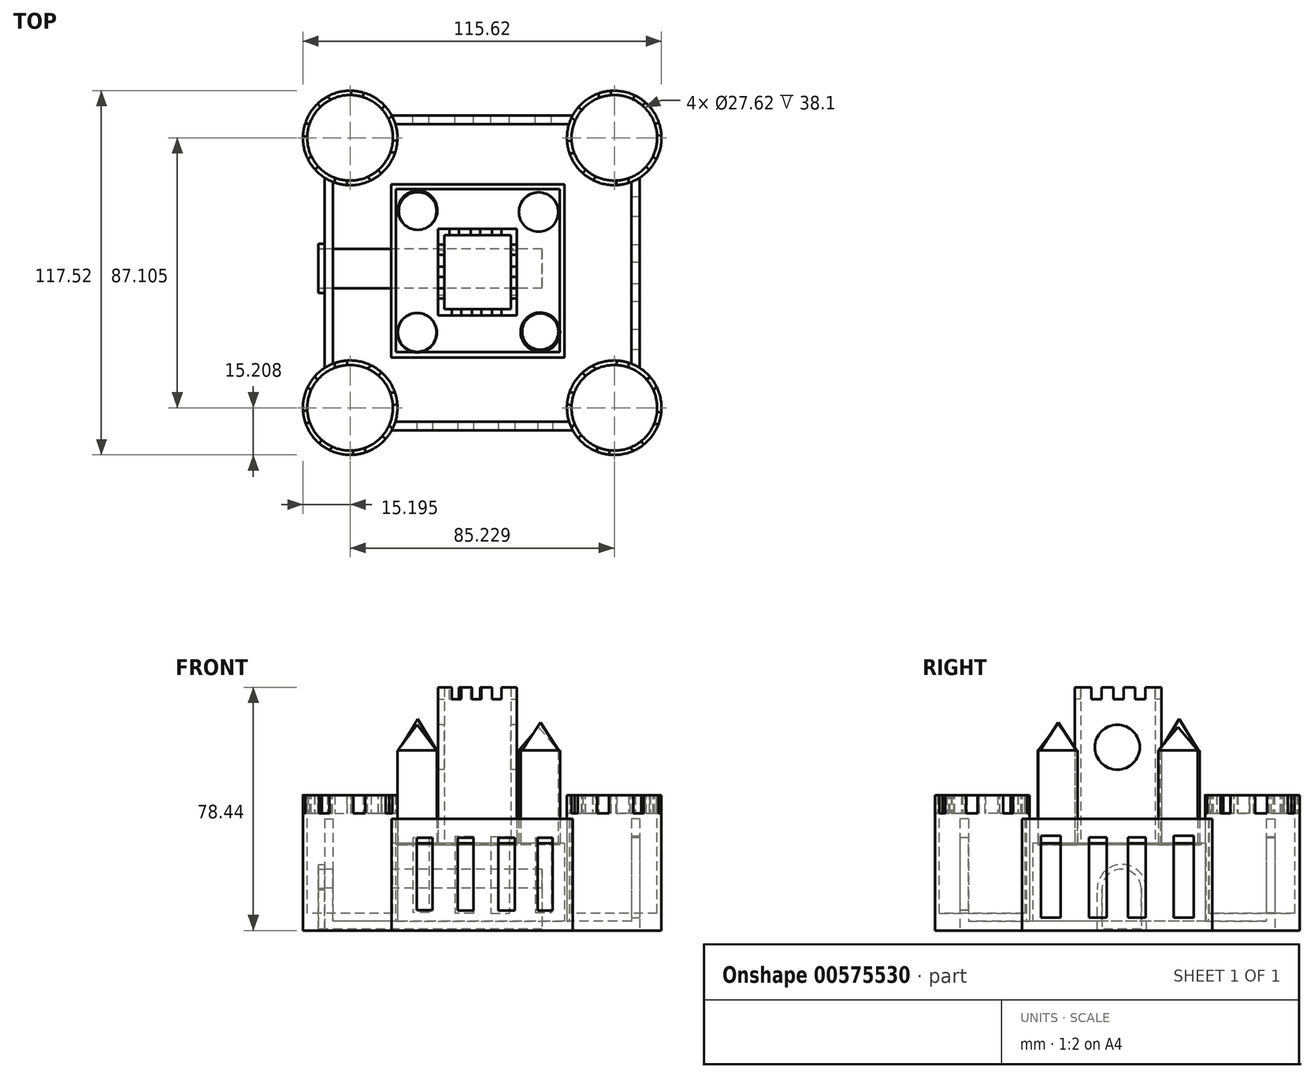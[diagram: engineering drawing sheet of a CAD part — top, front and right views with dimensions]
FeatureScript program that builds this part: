
annotation { "Feature Type Name" : "Feature", "Feature Type Description" : "" }
export const myFeature = defineFeature(function(context is Context, id is Id, definition is map)
    precondition{}
    {
        {
            var Q0;
            Q0=qCreatedBy(makeId("Top.planeOp"),FACE);
            var sketch = newSketch(context, id + "F0", { "sketchPlane" : qUnion([Q0])});
            skLineSegment(sketch, "E0.bottom", {"start": v(29.19, -50.8) * mm, "end": v(-29.19, -50.8) * mm});
            skLineSegment(sketch, "E0.top", {"start": v(29.19, 50.8) * mm, "end": v(-29.19, 50.8) * mm});
            skLineSegment(sketch, "E0.left", {"start": v(50.8, -30.7) * mm, "end": v(50.8, 30.7) * mm});
            skLineSegment(sketch, "E0.right", {"start": v(-50.8, -30.7) * mm, "end": v(-50.8, 30.7) * mm});
            skPoint(sketch, "E0.middle", {"position": v(0, 0) * mm});
            skCircle(sketch, "E1", {"center": v(-42.57, 43.52) * mm, "radius": 15.24 * mm});
            skCircle(sketch, "E2.MirrorC", {"center": v(42.57, 43.52) * mm, "radius": 15.24 * mm});
            skCircle(sketch, "E3.MirrorC", {"center": v(-42.57, -43.52) * mm, "radius": 15.24 * mm});
            skCircle(sketch, "E4.MirrorC", {"center": v(42.57, -43.52) * mm, "radius": 15.24 * mm});
            skPoint(sketch, "E5.orphan", {"position": v(-50.8, 50.8) * mm});
            skPoint(sketch, "E6.orphan", {"position": v(-50.8, -50.8) * mm});
            skPoint(sketch, "E7.orphan", {"position": v(50.8, -50.8) * mm});
            skPoint(sketch, "E8.orphan", {"position": v(50.8, 50.8) * mm});
            skSolve(sketch);
        }
        {
            var Q0;
            Q0 = qSketchRegion(id + "F0", true);
            extrude(context, id + "F1", {"entities" : qUnion([Q0]), "depth" : 3 * mm, "offsetDistance" : 25.4 * mm});
        }
        {
            var Q0;
            Q0=makeQuery(id+"F1.opExtrude","CAP_FACE",FACE,{"disambiguationData":[OSD([sQuery(id+"F0.wireOp",EDGE,"E0.bottom"),sQuery(id+"F0.wireOp",EDGE,"E0.top"),sQuery(id+"F0.wireOp",EDGE,"E0.left"),sQuery(id+"F0.wireOp",EDGE,"E0.right"),sQuery(id+"F0.wireOp",EDGE,"E1"),sQuery(id+"F0.wireOp",EDGE,"E2.MirrorC"),sQuery(id+"F0.wireOp",EDGE,"E3.MirrorC"),sQuery(id+"F0.wireOp",EDGE,"E4.MirrorC")])],"isStart":false});
            var sketch = newSketch(context, id + "F2", { "sketchPlane" : qUnion([Q0])});
            skCircle(sketch, "E9", {"center": v(-42.57, 43.52) * mm, "radius": 15.24 * mm});
            skCircle(sketch, "E10.MirrorC", {"center": v(42.57, 43.52) * mm, "radius": 15.24 * mm});
            skCircle(sketch, "E11.MirrorC", {"center": v(-42.57, -43.52) * mm, "radius": 15.24 * mm});
            skCircle(sketch, "E12.MirrorC", {"center": v(42.57, -43.52) * mm, "radius": 15.24 * mm});
            skSolve(sketch);
        }
        {
            var Q0;
            Q0 = qSketchRegion(id + "F2", true);
            extrude(context, id + "F3", {"entities" : qUnion([Q0]), "operationType" : NewBodyOperationType.ADD, "depth" : 40.64 * mm, "offsetDistance" : 25.4 * mm});
        }
        {
            var Q0;
            Q0=makeQuery(id+"F1.opExtrude","CAP_FACE",FACE,{"disambiguationData":[OSD([sQuery(id+"F0.wireOp",EDGE,"E0.bottom"),sQuery(id+"F0.wireOp",EDGE,"E0.top"),sQuery(id+"F0.wireOp",EDGE,"E0.left"),sQuery(id+"F0.wireOp",EDGE,"E0.right"),sQuery(id+"F0.wireOp",EDGE,"E1"),sQuery(id+"F0.wireOp",EDGE,"E2.MirrorC"),sQuery(id+"F0.wireOp",EDGE,"E3.MirrorC"),sQuery(id+"F0.wireOp",EDGE,"E4.MirrorC")])],"isStart":false});
            var sketch = newSketch(context, id + "F4", { "sketchPlane" : qUnion([Q0])});
            skArc(sketch, "E13", {"start": v(-29.19, -50.8) * mm, "mid": v(-28.53, -49.45) * mm, "end": v(-28.02, -48.04) * mm});
            skArc(sketch, "E14.MirrorCS", {"start": v(29.19, -50.8) * mm, "mid": v(28.53, -49.45) * mm, "end": v(28.02, -48.04) * mm});
            skLineSegment(sketch, "E15", {"start": v(-29.19, -50.8) * mm, "end": v(29.19, -50.8) * mm});
            skLineSegment(sketch, "E16", {"start": v(-28.02, -48.04) * mm, "end": v(28.02, -48.04) * mm});
            skLineSegment(sketch, "E17.MirrorCS", {"start": v(-28.02, 48.04) * mm, "end": v(28.02, 48.04) * mm});
            skLineSegment(sketch, "E18.MirrorCS", {"start": v(-29.19, 50.8) * mm, "end": v(29.19, 50.8) * mm});
            skArc(sketch, "E19.MirrorCS", {"start": v(29.19, 50.8) * mm, "mid": v(28.53, 49.45) * mm, "end": v(28.02, 48.04) * mm});
            skArc(sketch, "E20.MirrorCS", {"start": v(-29.19, 50.8) * mm, "mid": v(-28.53, 49.45) * mm, "end": v(-28.02, 48.04) * mm});
            skArc(sketch, "E21.trimOffspring", {"start": v(-48.13, -29.33) * mm, "mid": v(-49.5, -29.94) * mm, "end": v(-50.8, -30.7) * mm});
            skArc(sketch, "E22.MirrorCS", {"start": v(-48.13, 29.33) * mm, "mid": v(-49.5, 29.94) * mm, "end": v(-50.8, 30.7) * mm});
            skLineSegment(sketch, "E23", {"start": v(-50.8, 30.7) * mm, "end": v(-50.8, -30.7) * mm});
            skLineSegment(sketch, "E24", {"start": v(-48.13, 29.33) * mm, "end": v(-48.13, -29.33) * mm});
            skLineSegment(sketch, "E25.MirrorCS", {"start": v(48.13, 29.33) * mm, "end": v(48.13, -29.33) * mm});
            skLineSegment(sketch, "E26.MirrorCS", {"start": v(50.8, 30.7) * mm, "end": v(50.8, -30.7) * mm});
            skArc(sketch, "E27.MirrorCS", {"start": v(48.13, -29.33) * mm, "mid": v(49.5, -29.94) * mm, "end": v(50.8, -30.7) * mm});
            skArc(sketch, "E28.MirrorCS", {"start": v(48.13, 29.33) * mm, "mid": v(49.5, 29.94) * mm, "end": v(50.8, 30.7) * mm});
            skSolve(sketch);
        }
        {
            var Q0;
            Q0 = qSketchRegion(id + "F4", true);
            extrude(context, id + "F5", {"entities" : qUnion([Q0]), "operationType" : NewBodyOperationType.ADD, "depth" : 33.02 * mm, "offsetDistance" : 25.4 * mm});
        }
        {
            var Q0;
            Q0=makeQuery(id+"F3.opExtrude","CAP_FACE",FACE,{"disambiguationData":[OSD([sQuery(id+"F2.wireOp",EDGE,"E10.MirrorC")])],"isStart":false});
            var sketch = newSketch(context, id + "F6", { "sketchPlane" : qUnion([Q0])});
            skPoint(sketch, "E29.first.point", {"position": v(-57.88, 42.89) * mm});
            skPoint(sketch, "E29.second.point", {"position": v(-27.36, 44.4) * mm});
            skPoint(sketch, "E29.third.point", {"position": v(-44.7, 28.42) * mm});
            skCircle(sketch, "E30", {"center": v(-42.61, 43.55) * mm, "radius": 13.8 * mm});
            skCircle(sketch, "E31.MirrorC", {"center": v(-42.61, -43.55) * mm, "radius": 13.8 * mm});
            skCircle(sketch, "E32.MirrorC", {"center": v(42.61, 43.55) * mm, "radius": 13.8 * mm});
            skCircle(sketch, "E33.MirrorC", {"center": v(42.61, -43.55) * mm, "radius": 13.8 * mm});
            skSolve(sketch);
        }
        {
            var Q0;
            Q0 = qSketchRegion(id + "F6", true);
            extrude(context, id + "F7", {"entities" : qUnion([Q0]), "operationType" : NewBodyOperationType.REMOVE, "oppositeDirection" : true, "depth" : 38.1 * mm, "offsetDistance" : 25.4 * mm});
        }
        {
            var Q0;
            Q0=makeQuery(id+"F3.opExtrude","CAP_FACE",FACE,{"disambiguationData":[OSD([sQuery(id+"F2.wireOp",EDGE,"E11.MirrorC")])],"isStart":false});
            var sketch = newSketch(context, id + "F8", { "sketchPlane" : qUnion([Q0])});
            skLineSegment(sketch, "E34", {"start": v(-47.54, -28.27) * mm, "end": v(-47.54, -31.48) * mm});
            skLineSegment(sketch, "E35", {"start": v(-47.54, -31.48) * mm, "end": v(-43.3, -30.83) * mm});
            skLineSegment(sketch, "E36", {"start": v(-43.3, -30.83) * mm, "end": v(-43.78, -27.75) * mm});
            skLineSegment(sketch, "E37", {"start": v(-43.78, -27.75) * mm, "end": v(-47.54, -28.27) * mm});
            skLineSegment(sketch, "E38.1.0", {"start": v(-54.6, -33.2) * mm, "end": v(-56.9, -36.23) * mm});
            skLineSegment(sketch, "E38.1.1", {"start": v(-54.63, -38.5) * mm, "end": v(-52.1, -35.05) * mm});
            skLineSegment(sketch, "E38.1.2", {"start": v(-56.9, -36.23) * mm, "end": v(-54.63, -38.5) * mm});
            skLineSegment(sketch, "E38.1.3", {"start": v(-52.1, -35.05) * mm, "end": v(-54.6, -33.2) * mm});
            skLineSegment(sketch, "E38.2.0", {"start": v(-58.41, -44.72) * mm, "end": v(-57.9, -48.48) * mm});
            skLineSegment(sketch, "E38.2.1", {"start": v(-54.68, -48.48) * mm, "end": v(-55.33, -44.24) * mm});
            skLineSegment(sketch, "E38.2.2", {"start": v(-57.9, -48.48) * mm, "end": v(-54.68, -48.48) * mm});
            skLineSegment(sketch, "E38.2.3", {"start": v(-55.33, -44.24) * mm, "end": v(-58.41, -44.72) * mm});
            skLineSegment(sketch, "E38.3.0", {"start": v(-52.96, -55.55) * mm, "end": v(-49.94, -57.84) * mm});
            skLineSegment(sketch, "E38.3.1", {"start": v(-47.67, -55.57) * mm, "end": v(-51.12, -53.03) * mm});
            skLineSegment(sketch, "E38.3.2", {"start": v(-49.94, -57.84) * mm, "end": v(-47.67, -55.57) * mm});
            skLineSegment(sketch, "E38.3.3", {"start": v(-51.12, -53.03) * mm, "end": v(-52.96, -55.55) * mm});
            skLineSegment(sketch, "E38.4.0", {"start": v(-41.45, -59.35) * mm, "end": v(-37.69, -58.83) * mm});
            skLineSegment(sketch, "E38.4.1", {"start": v(-37.69, -55.62) * mm, "end": v(-41.92, -56.27) * mm});
            skLineSegment(sketch, "E38.4.2", {"start": v(-37.69, -58.83) * mm, "end": v(-37.69, -55.62) * mm});
            skLineSegment(sketch, "E38.4.3", {"start": v(-41.92, -56.27) * mm, "end": v(-41.45, -59.35) * mm});
            skLineSegment(sketch, "E38.5.0", {"start": v(-30.62, -53.9) * mm, "end": v(-28.33, -50.87) * mm});
            skLineSegment(sketch, "E38.5.1", {"start": v(-30.6, -48.6) * mm, "end": v(-33.13, -52.06) * mm});
            skLineSegment(sketch, "E38.5.2", {"start": v(-28.33, -50.87) * mm, "end": v(-30.6, -48.6) * mm});
            skLineSegment(sketch, "E38.5.3", {"start": v(-33.13, -52.06) * mm, "end": v(-30.62, -53.9) * mm});
            skLineSegment(sketch, "E38.6.0", {"start": v(-26.82, -42.39) * mm, "end": v(-27.33, -38.63) * mm});
            skLineSegment(sketch, "E38.6.1", {"start": v(-30.55, -38.63) * mm, "end": v(-29.9, -42.86) * mm});
            skLineSegment(sketch, "E38.6.2", {"start": v(-27.33, -38.63) * mm, "end": v(-30.55, -38.63) * mm});
            skLineSegment(sketch, "E38.6.3", {"start": v(-29.9, -42.86) * mm, "end": v(-26.82, -42.39) * mm});
            skLineSegment(sketch, "E38.7.0", {"start": v(-32.27, -31.56) * mm, "end": v(-35.3, -29.26) * mm});
            skLineSegment(sketch, "E38.7.1", {"start": v(-37.56, -31.54) * mm, "end": v(-34.1, -34.07) * mm});
            skLineSegment(sketch, "E38.7.2", {"start": v(-35.3, -29.26) * mm, "end": v(-37.56, -31.54) * mm});
            skLineSegment(sketch, "E38.7.3", {"start": v(-34.1, -34.07) * mm, "end": v(-32.27, -31.56) * mm});
            skPoint(sketch, "E38.center", {"position": v(-42.61, -43.55) * mm});
            skLineSegment(sketch, "E39.MirrorCS", {"start": v(-47.54, 31.48) * mm, "end": v(-43.3, 30.83) * mm});
            skLineSegment(sketch, "E40.MirrorCS", {"start": v(-43.78, 27.75) * mm, "end": v(-47.54, 28.27) * mm});
            skLineSegment(sketch, "E41.MirrorCS", {"start": v(-43.3, 30.83) * mm, "end": v(-43.78, 27.75) * mm});
            skLineSegment(sketch, "E42.MirrorCS", {"start": v(-47.54, 28.27) * mm, "end": v(-47.54, 31.48) * mm});
            skLineSegment(sketch, "E43.MirrorCS", {"start": v(26.82, -42.39) * mm, "end": v(27.33, -38.63) * mm});
            skLineSegment(sketch, "E44.MirrorCS", {"start": v(30.55, -38.63) * mm, "end": v(29.9, -42.86) * mm});
            skLineSegment(sketch, "E45.MirrorCS", {"start": v(29.9, -42.86) * mm, "end": v(26.82, -42.39) * mm});
            skLineSegment(sketch, "E46.MirrorCS", {"start": v(27.33, -38.63) * mm, "end": v(30.55, -38.63) * mm});
            skLineSegment(sketch, "E47.MirrorCS", {"start": v(27.33, 38.63) * mm, "end": v(30.55, 38.63) * mm});
            skLineSegment(sketch, "E48.MirrorCS", {"start": v(29.9, 42.86) * mm, "end": v(26.82, 42.39) * mm});
            skLineSegment(sketch, "E49.MirrorCS", {"start": v(30.55, 38.63) * mm, "end": v(29.9, 42.86) * mm});
            skLineSegment(sketch, "E50.MirrorCS", {"start": v(26.82, 42.39) * mm, "end": v(27.33, 38.63) * mm});
            skLineSegment(sketch, "E51.1.0", {"start": v(32.9, -51.78) * mm, "end": v(30.4, -53.62) * mm});
            skLineSegment(sketch, "E51.1.1", {"start": v(30.4, -53.62) * mm, "end": v(28.1, -50.6) * mm});
            skLineSegment(sketch, "E51.1.2", {"start": v(30.37, -48.32) * mm, "end": v(32.9, -51.78) * mm});
            skLineSegment(sketch, "E51.1.3", {"start": v(28.1, -50.6) * mm, "end": v(30.37, -48.32) * mm});
            skLineSegment(sketch, "E51.2.0", {"start": v(41.34, -55.96) * mm, "end": v(40.87, -59.04) * mm});
            skLineSegment(sketch, "E51.2.1", {"start": v(40.87, -59.04) * mm, "end": v(37.1, -58.52) * mm});
            skLineSegment(sketch, "E51.2.2", {"start": v(37.1, -55.3) * mm, "end": v(41.34, -55.96) * mm});
            skLineSegment(sketch, "E51.2.3", {"start": v(37.1, -58.52) * mm, "end": v(37.1, -55.3) * mm});
            skLineSegment(sketch, "E51.3.0", {"start": v(50.26, -52.95) * mm, "end": v(52.1, -55.46) * mm});
            skLineSegment(sketch, "E51.3.1", {"start": v(52.1, -55.46) * mm, "end": v(49.07, -57.75) * mm});
            skLineSegment(sketch, "E51.3.2", {"start": v(46.8, -55.48) * mm, "end": v(50.26, -52.95) * mm});
            skLineSegment(sketch, "E51.3.3", {"start": v(49.07, -57.75) * mm, "end": v(46.8, -55.48) * mm});
            skLineSegment(sketch, "E51.4.0", {"start": v(54.43, -44.51) * mm, "end": v(57.51, -44.99) * mm});
            skLineSegment(sketch, "E51.4.2", {"start": v(53.78, -48.75) * mm, "end": v(54.43, -44.51) * mm});
            skLineSegment(sketch, "E51.4.3", {"start": v(57, -48.75) * mm, "end": v(53.78, -48.75) * mm});
            skLineSegment(sketch, "E51.5.0", {"start": v(51.42, -35.6) * mm, "end": v(53.93, -33.75) * mm});
            skLineSegment(sketch, "E51.5.2", {"start": v(53.96, -39.05) * mm, "end": v(51.42, -35.6) * mm});
            skLineSegment(sketch, "E51.5.3", {"start": v(56.23, -36.78) * mm, "end": v(53.96, -39.05) * mm});
            skLineSegment(sketch, "E51.6.0", {"start": v(42.99, -31.42) * mm, "end": v(43.46, -28.34) * mm});
            skLineSegment(sketch, "E51.6.2", {"start": v(47.23, -32.07) * mm, "end": v(42.99, -31.42) * mm});
            skLineSegment(sketch, "E51.6.3", {"start": v(47.23, -28.86) * mm, "end": v(47.23, -32.07) * mm});
            skLineSegment(sketch, "E51.7.0", {"start": v(34.07, -34.43) * mm, "end": v(32.23, -31.92) * mm});
            skLineSegment(sketch, "E51.7.1", {"start": v(32.23, -31.92) * mm, "end": v(35.26, -29.62) * mm});
            skLineSegment(sketch, "E51.7.2", {"start": v(37.53, -31.9) * mm, "end": v(34.07, -34.43) * mm});
            skLineSegment(sketch, "E51.7.3", {"start": v(35.26, -29.62) * mm, "end": v(37.53, -31.9) * mm});
            skPoint(sketch, "E51.center", {"position": v(42.16, -43.69) * mm});
            skLineSegment(sketch, "E52.1.0", {"start": v(32.12, 31.66) * mm, "end": v(35.15, 29.37) * mm});
            skLineSegment(sketch, "E52.1.1", {"start": v(37.42, 31.64) * mm, "end": v(33.97, 34.17) * mm});
            skLineSegment(sketch, "E52.1.2", {"start": v(33.97, 34.17) * mm, "end": v(32.12, 31.66) * mm});
            skLineSegment(sketch, "E52.1.3", {"start": v(35.15, 29.37) * mm, "end": v(37.42, 31.64) * mm});
            skLineSegment(sketch, "E52.2.0", {"start": v(43.46, 27.83) * mm, "end": v(47.23, 28.35) * mm});
            skLineSegment(sketch, "E52.2.1", {"start": v(47.23, 31.56) * mm, "end": v(42.99, 30.91) * mm});
            skLineSegment(sketch, "E52.2.2", {"start": v(42.99, 30.91) * mm, "end": v(43.46, 27.83) * mm});
            skLineSegment(sketch, "E52.2.3", {"start": v(47.23, 28.35) * mm, "end": v(47.23, 31.56) * mm});
            skLineSegment(sketch, "E52.3.0", {"start": v(54.19, 33.14) * mm, "end": v(56.48, 36.17) * mm});
            skLineSegment(sketch, "E52.3.1", {"start": v(54.21, 38.44) * mm, "end": v(51.68, 34.98) * mm});
            skLineSegment(sketch, "E52.3.2", {"start": v(51.68, 34.98) * mm, "end": v(54.19, 33.14) * mm});
            skLineSegment(sketch, "E52.3.3", {"start": v(56.48, 36.17) * mm, "end": v(54.21, 38.44) * mm});
            skLineSegment(sketch, "E52.4.0", {"start": v(58.02, 44.48) * mm, "end": v(57.5, 48.24) * mm});
            skLineSegment(sketch, "E52.4.1", {"start": v(54.3, 48.24) * mm, "end": v(54.94, 44) * mm});
            skLineSegment(sketch, "E52.4.2", {"start": v(54.94, 44) * mm, "end": v(58.02, 44.48) * mm});
            skLineSegment(sketch, "E52.4.3", {"start": v(57.5, 48.24) * mm, "end": v(54.3, 48.24) * mm});
            skLineSegment(sketch, "E52.5.0", {"start": v(52.71, 55.2) * mm, "end": v(49.68, 57.5) * mm});
            skLineSegment(sketch, "E52.5.1", {"start": v(47.41, 55.23) * mm, "end": v(50.87, 52.7) * mm});
            skLineSegment(sketch, "E52.5.2", {"start": v(50.87, 52.7) * mm, "end": v(52.71, 55.2) * mm});
            skLineSegment(sketch, "E52.5.3", {"start": v(49.68, 57.5) * mm, "end": v(47.41, 55.23) * mm});
            skLineSegment(sketch, "E52.6.0", {"start": v(41.37, 59.04) * mm, "end": v(37.61, 58.52) * mm});
            skLineSegment(sketch, "E52.6.1", {"start": v(37.61, 55.3) * mm, "end": v(41.85, 55.96) * mm});
            skLineSegment(sketch, "E52.6.2", {"start": v(41.85, 55.96) * mm, "end": v(41.37, 59.04) * mm});
            skLineSegment(sketch, "E52.6.3", {"start": v(37.61, 58.52) * mm, "end": v(37.61, 55.3) * mm});
            skLineSegment(sketch, "E52.7.0", {"start": v(30.65, 53.73) * mm, "end": v(28.35, 50.7) * mm});
            skLineSegment(sketch, "E52.7.1", {"start": v(30.62, 48.43) * mm, "end": v(33.16, 51.89) * mm});
            skLineSegment(sketch, "E52.7.2", {"start": v(33.16, 51.89) * mm, "end": v(30.65, 53.73) * mm});
            skLineSegment(sketch, "E52.7.3", {"start": v(28.35, 50.7) * mm, "end": v(30.62, 48.43) * mm});
            skPoint(sketch, "E52.center", {"position": v(42.42, 43.43) * mm});
            skLineSegment(sketch, "E53.1.0", {"start": v(-35.47, 29.45) * mm, "end": v(-37.74, 31.72) * mm});
            skLineSegment(sketch, "E53.1.1", {"start": v(-34.28, 34.26) * mm, "end": v(-32.44, 31.74) * mm});
            skLineSegment(sketch, "E53.1.2", {"start": v(-32.44, 31.74) * mm, "end": v(-35.47, 29.45) * mm});
            skLineSegment(sketch, "E53.1.3", {"start": v(-37.74, 31.72) * mm, "end": v(-34.28, 34.26) * mm});
            skLineSegment(sketch, "E53.2.0", {"start": v(-27.76, 38.82) * mm, "end": v(-30.98, 38.82) * mm});
            skLineSegment(sketch, "E53.2.1", {"start": v(-30.32, 43.06) * mm, "end": v(-27.25, 42.58) * mm});
            skLineSegment(sketch, "E53.2.2", {"start": v(-27.25, 42.58) * mm, "end": v(-27.76, 38.82) * mm});
            skLineSegment(sketch, "E53.2.3", {"start": v(-30.98, 38.82) * mm, "end": v(-30.32, 43.06) * mm});
            skLineSegment(sketch, "E53.3.0", {"start": v(-28.94, 50.9) * mm, "end": v(-31.21, 48.62) * mm});
            skLineSegment(sketch, "E53.3.1", {"start": v(-33.75, 52.08) * mm, "end": v(-31.24, 53.92) * mm});
            skLineSegment(sketch, "E53.3.2", {"start": v(-31.24, 53.92) * mm, "end": v(-28.94, 50.9) * mm});
            skLineSegment(sketch, "E53.3.3", {"start": v(-31.21, 48.62) * mm, "end": v(-33.75, 52.08) * mm});
            skLineSegment(sketch, "E53.4.0", {"start": v(-38.31, 58.6) * mm, "end": v(-38.31, 55.38) * mm});
            skLineSegment(sketch, "E53.4.1", {"start": v(-42.55, 56.04) * mm, "end": v(-42.07, 59.11) * mm});
            skLineSegment(sketch, "E53.4.2", {"start": v(-42.07, 59.11) * mm, "end": v(-38.31, 58.6) * mm});
            skLineSegment(sketch, "E53.4.3", {"start": v(-38.31, 55.38) * mm, "end": v(-42.55, 56.04) * mm});
            skLineSegment(sketch, "E53.5.0", {"start": v(-50.38, 57.42) * mm, "end": v(-48.11, 55.15) * mm});
            skLineSegment(sketch, "E53.5.1", {"start": v(-51.57, 52.61) * mm, "end": v(-53.41, 55.12) * mm});
            skLineSegment(sketch, "E53.5.2", {"start": v(-53.41, 55.12) * mm, "end": v(-50.38, 57.42) * mm});
            skLineSegment(sketch, "E53.5.3", {"start": v(-48.11, 55.15) * mm, "end": v(-51.57, 52.61) * mm});
            skLineSegment(sketch, "E53.6.0", {"start": v(-58.09, 48.05) * mm, "end": v(-54.88, 48.05) * mm});
            skLineSegment(sketch, "E53.6.1", {"start": v(-55.53, 43.81) * mm, "end": v(-58.6, 44.29) * mm});
            skLineSegment(sketch, "E53.6.2", {"start": v(-58.6, 44.29) * mm, "end": v(-58.09, 48.05) * mm});
            skLineSegment(sketch, "E53.6.3", {"start": v(-54.88, 48.05) * mm, "end": v(-55.53, 43.81) * mm});
            skLineSegment(sketch, "E53.7.0", {"start": v(-56.9, 35.98) * mm, "end": v(-54.64, 38.25) * mm});
            skLineSegment(sketch, "E53.7.1", {"start": v(-52.1, 34.8) * mm, "end": v(-54.62, 32.95) * mm});
            skLineSegment(sketch, "E53.7.2", {"start": v(-54.62, 32.95) * mm, "end": v(-56.9, 35.98) * mm});
            skLineSegment(sketch, "E53.7.3", {"start": v(-54.64, 38.25) * mm, "end": v(-52.1, 34.8) * mm});
            skPoint(sketch, "E53.center", {"position": v(-42.93, 43.43) * mm});
            skLineSegment(sketch, "E54", {"start": v(57, -48.75) * mm, "end": v(60.9, -48.75) * mm});
            skLineSegment(sketch, "E55", {"start": v(60.9, -48.75) * mm, "end": v(60.87, -45.44) * mm});
            skLineSegment(sketch, "E56", {"start": v(60.87, -45.44) * mm, "end": v(57.51, -44.99) * mm});
            skLineSegment(sketch, "E57", {"start": v(56.23, -36.78) * mm, "end": v(62.09, -33.6) * mm});
            skLineSegment(sketch, "E58", {"start": v(62.09, -33.6) * mm, "end": v(58.77, -31.36) * mm});
            skLineSegment(sketch, "E59", {"start": v(58.77, -31.36) * mm, "end": v(53.93, -33.75) * mm});
            skLineSegment(sketch, "E60", {"start": v(47.23, -28.86) * mm, "end": v(43.42, -20.08) * mm});
            skLineSegment(sketch, "E61", {"start": v(43.42, -20.08) * mm, "end": v(43.46, -28.34) * mm});
            skSolve(sketch);
        }
        {
            var Q0;
            Q0 = qSketchRegion(id + "F8", true);
            extrude(context, id + "F9", {"entities" : qUnion([Q0]), "operationType" : NewBodyOperationType.REMOVE, "oppositeDirection" : true, "depth" : 5.84 * mm, "offsetDistance" : 25.4 * mm});
        }
        {
            var Q0;
            Q0=makeQuery(id+"F1.opExtrude","CAP_FACE",FACE,{"disambiguationData":[OSD([sQuery(id+"F0.wireOp",EDGE,"E0.bottom"),sQuery(id+"F0.wireOp",EDGE,"E0.top"),sQuery(id+"F0.wireOp",EDGE,"E0.left"),sQuery(id+"F0.wireOp",EDGE,"E0.right"),sQuery(id+"F0.wireOp",EDGE,"E1"),sQuery(id+"F0.wireOp",EDGE,"E2.MirrorC"),sQuery(id+"F0.wireOp",EDGE,"E3.MirrorC"),sQuery(id+"F0.wireOp",EDGE,"E4.MirrorC")])],"isStart":false});
            var sketch = newSketch(context, id + "F10", { "sketchPlane" : qUnion([Q0])});
            skLineSegment(sketch, "E62.bottom", {"start": v(26.57, 28.58) * mm, "end": v(-29.31, 28.58) * mm});
            skLineSegment(sketch, "E62.top", {"start": v(26.57, -27.3) * mm, "end": v(-29.31, -27.3) * mm});
            skLineSegment(sketch, "E62.left", {"start": v(26.57, 28.58) * mm, "end": v(26.57, -27.3) * mm});
            skLineSegment(sketch, "E62.right", {"start": v(-29.31, 28.58) * mm, "end": v(-29.31, -27.3) * mm});
            skSolve(sketch);
        }
        {
            var Q0;
            Q0 = qSketchRegion(id + "F10", true);
            extrude(context, id + "F11", {"entities" : qUnion([Q0]), "operationType" : NewBodyOperationType.ADD, "depth" : 24.64 * mm, "offsetDistance" : 25.4 * mm});
        }
        {
            var Q0;
            Q0=makeQuery(id+"F5.boolean.opBoolean","MERGE",FACE,{"derivedFrom":[makeQuery(id+"F1.opExtrude","SWEPT_FACE",FACE,{"disambiguationData":[OSD([sQuery(id+"F0.wireOp",EDGE,"E0.right")])]}),makeQuery(id+"F5.opExtrude","SWEPT_FACE",FACE,{"disambiguationData":[OSD([sQuery(id+"F4.wireOp",EDGE,"E23")])]})]});
            var sketch = newSketch(context, id + "F12", { "sketchPlane" : qUnion([Q0])});
            skLineSegment(sketch, "E63.left", {"start": v(-7.73, 13.66) * mm, "end": v(-7.73, 0.5) * mm});
            skLineSegment(sketch, "E63.right", {"start": v(4.97, 13.4) * mm, "end": v(4.97, 0.5) * mm});
            skArc(sketch, "E64", {"start": v(4.97, 13.4) * mm, "mid": v(-1.25, 19.76) * mm, "end": v(-7.73, 13.66) * mm});
            skLineSegment(sketch, "E65", {"start": v(-7.73, 0.5) * mm, "end": v(4.97, 0.5) * mm});
            skPoint(sketch, "E66.orphan", {"position": v(4.97, 0) * mm});
            skSolve(sketch);
        }
        {
            var Q0;
            Q0 = qSketchRegion(id + "F12", true);
            extrude(context, id + "F13", {"entities" : qUnion([Q0]), "operationType" : NewBodyOperationType.REMOVE, "oppositeDirection" : true, "depth" : 70.1 * mm, "offsetDistance" : 25.4 * mm});
        }
        {
            var Q0;
            Q0=makeQuery(id+"F11.opExtrude","CAP_FACE",FACE,{"disambiguationData":[OSD([sQuery(id+"F10.wireOp",EDGE,"E62.bottom"),sQuery(id+"F10.wireOp",EDGE,"E62.top"),sQuery(id+"F10.wireOp",EDGE,"E62.left"),sQuery(id+"F10.wireOp",EDGE,"E62.right")])],"isStart":false});
            var sketch = newSketch(context, id + "F14", { "sketchPlane" : qUnion([Q0])});
            skLineSegment(sketch, "E67.bottom", {"start": v(25.06, 27.01) * mm, "end": v(-27.79, 27.01) * mm});
            skLineSegment(sketch, "E67.top", {"start": v(25.06, -25.6) * mm, "end": v(-27.79, -25.6) * mm});
            skLineSegment(sketch, "E67.left", {"start": v(25.06, 27.01) * mm, "end": v(25.06, -25.6) * mm});
            skLineSegment(sketch, "E67.right", {"start": v(-27.79, 27.01) * mm, "end": v(-27.79, -25.6) * mm});
            skLineSegment(sketch, "E68.bottom", {"start": v(26.57, 28.58) * mm, "end": v(-29.31, 28.58) * mm});
            skLineSegment(sketch, "E68.top", {"start": v(26.57, -27.3) * mm, "end": v(-29.31, -27.3) * mm});
            skLineSegment(sketch, "E68.left", {"start": v(26.57, 28.58) * mm, "end": v(26.57, -27.3) * mm});
            skLineSegment(sketch, "E68.right", {"start": v(-29.31, 28.58) * mm, "end": v(-29.31, -27.3) * mm});
            skSolve(sketch);
        }
        {
            var Q0;
            Q0 = qSketchRegion(id + "F14", true);
            extrude(context, id + "F15", {"entities" : qUnion([Q0]), "operationType" : NewBodyOperationType.ADD, "depth" : 0.5 * mm, "offsetDistance" : 25.4 * mm});
        }
        {
            var Q0;
            Q0=qCreatedBy(makeId("Right.planeOp"),FACE);
            var sketch = newSketch(context, id + "F16", { "sketchPlane" : qUnion([Q0])});
            skLineSegment(sketch, "E69", {"start": v(0, 0) * mm, "end": v(0, 76.04) * mm, "construction": true});
            skSolve(sketch);
        }
        {
            var Q0;
            Q0=makeQuery(id+"F11.opExtrude","CAP_FACE",FACE,{"disambiguationData":[OSD([sQuery(id+"F10.wireOp",EDGE,"E62.bottom"),sQuery(id+"F10.wireOp",EDGE,"E62.top"),sQuery(id+"F10.wireOp",EDGE,"E62.left"),sQuery(id+"F10.wireOp",EDGE,"E62.right")])],"isStart":false});
            var sketch = newSketch(context, id + "F17", { "sketchPlane" : qUnion([Q0])});
            skCircle(sketch, "E70", {"center": v(18.2, 19.61) * mm, "radius": 6.35 * mm});
            skCircle(sketch, "E71", {"center": v(18.73, -19.13) * mm, "radius": 6.35 * mm});
            skCircle(sketch, "E72", {"center": v(-20.8, 20.22) * mm, "radius": 6.35 * mm});
            skCircle(sketch, "E73", {"center": v(-20.97, -19.33) * mm, "radius": 6.35 * mm});
            skSolve(sketch);
        }
        {
            var Q0;
            Q0 = qSketchRegion(id + "F17", true);
            extrude(context, id + "F18", {"entities" : qUnion([Q0]), "operationType" : NewBodyOperationType.ADD, "depth" : 30.48 * mm, "offsetDistance" : 25.4 * mm});
        }
        {
            var Q0;
            Q0=makeQuery(id+"F18.opExtrude","SWEPT_FACE",FACE,{"disambiguationData":[OSD([sQuery(id+"F17.wireOp",EDGE,"E73")])]});
            cPlane(context, id + "F19", {"entities" : qUnion([Q0]), "cplaneType" : CPlaneType.LINE_ANGLE, "offset" : 25.4 * mm, "angle" : 0 * degree, "width" : 152.4 * mm, "height" : 152.4 * mm});
        }
        {
            var Q0;
            Q0=qCreatedBy(id+"F19.planeOp",FACE);
            var sketch = newSketch(context, id + "F20", { "sketchPlane" : qUnion([Q0])});
            skLineSegment(sketch, "E74", {"start": v(19.24, 58.06) * mm, "end": v(19.24, 69.55) * mm, "construction": true});
            skLineSegment(sketch, "E75", {"start": v(19.24, 58.06) * mm, "end": v(25.54, 58.06) * mm});
            skLineSegment(sketch, "E76", {"start": v(25.54, 58.06) * mm, "end": v(19.24, 66.42) * mm});
            skLineSegment(sketch, "E77", {"start": v(19.24, 66.42) * mm, "end": v(19.24, 58.06) * mm});
            skSolve(sketch);
        }
        {
            var Q0;
            Q0 = qSketchRegion(id + "F20", true);
            var Q1;
            Q1=sQuery(id+"F20.wireOp",EDGE,"E74");
            revolve(context, id + "F21", {"operationType" : NewBodyOperationType.ADD, "entities" : qUnion([Q0]), "axis" : qUnion([Q1]), "revolveType" : RevolveType.FULL});
        }
        {
            var Q0;
            Q0=makeQuery(id+"F18.opExtrude","SWEPT_FACE",FACE,{"disambiguationData":[OSD([sQuery(id+"F17.wireOp",EDGE,"E71")])]});
            cPlane(context, id + "F22", {"entities" : qUnion([Q0]), "cplaneType" : CPlaneType.LINE_ANGLE, "offset" : 25.4 * mm, "angle" : 0 * degree, "width" : 152.4 * mm, "height" : 152.4 * mm});
        }
        {
            var Q0;
            Q0=qCreatedBy(id+"F22.planeOp",FACE);
            var sketch = newSketch(context, id + "F23", { "sketchPlane" : qUnion([Q0])});
            skLineSegment(sketch, "E78", {"start": v(18.97, 57.68) * mm, "end": v(18.97, 74.41) * mm, "construction": true});
            skLineSegment(sketch, "E79", {"start": v(18.97, 66.04) * mm, "end": v(18.97, 57.68) * mm});
            skLineSegment(sketch, "E80", {"start": v(18.97, 57.68) * mm, "end": v(12.84, 57.68) * mm});
            skLineSegment(sketch, "E81", {"start": v(12.84, 57.68) * mm, "end": v(18.97, 67.17) * mm});
            skLineSegment(sketch, "E82", {"start": v(18.97, 67.17) * mm, "end": v(18.97, 66.04) * mm});
            skSolve(sketch);
        }
        {
            var Q0;
            Q0 = qSketchRegion(id + "F23", true);
            var Q1;
            Q1=sQuery(id+"F23.wireOp",EDGE,"E79");
            revolve(context, id + "F24", {"operationType" : NewBodyOperationType.ADD, "entities" : qUnion([Q0]), "axis" : qUnion([Q1]), "revolveType" : RevolveType.FULL});
        }
        {
            var Q0;
            Q0=makeQuery(id+"F18.opExtrude","SWEPT_FACE",FACE,{"disambiguationData":[OSD([sQuery(id+"F17.wireOp",EDGE,"E72")])]});
            cPlane(context, id + "F25", {"entities" : qUnion([Q0]), "cplaneType" : CPlaneType.LINE_ANGLE, "offset" : 25.4 * mm, "angle" : 0 * degree, "width" : 152.4 * mm, "height" : 152.4 * mm});
        }
        {
            var Q0;
            Q0=qCreatedBy(id+"F25.planeOp",FACE);
            var sketch = newSketch(context, id + "F26", { "sketchPlane" : qUnion([Q0])});
            skLineSegment(sketch, "E83", {"start": v(-19.96, 58.3) * mm, "end": v(-19.96, 75.41) * mm, "construction": true});
            skLineSegment(sketch, "E84", {"start": v(-19.96, 58.3) * mm, "end": v(-13.86, 58.3) * mm});
            skLineSegment(sketch, "E85", {"start": v(-13.86, 58.3) * mm, "end": v(-19.96, 68.23) * mm});
            skLineSegment(sketch, "E86", {"start": v(-19.96, 68.23) * mm, "end": v(-19.96, 58.3) * mm});
            skSolve(sketch);
        }
        {
            var Q0;
            Q0 = qSketchRegion(id + "F26", true);
            var Q1;
            Q1=sQuery(id+"F26.wireOp",EDGE,"E83");
            revolve(context, id + "F27", {"entities" : qUnion([Q0]), "axis" : qUnion([Q1]), "revolveType" : RevolveType.FULL});
        }
        {
            var Q0;
            Q0=makeQuery(id+"F18.opExtrude","SWEPT_FACE",FACE,{"disambiguationData":[OSD([sQuery(id+"F17.wireOp",EDGE,"E70")])]});
            cPlane(context, id + "F28", {"entities" : qUnion([Q0]), "cplaneType" : CPlaneType.LINE_ANGLE, "offset" : 25.4 * mm, "angle" : 0 * degree, "width" : 152.4 * mm, "height" : 152.4 * mm});
        }
        {
            var Q0;
            Q0=qCreatedBy(id+"F28.planeOp",FACE);
            var sketch = newSketch(context, id + "F29", { "sketchPlane" : qUnion([Q0])});
            skLineSegment(sketch, "E87", {"start": v(-19.6, 58.15) * mm, "end": v(-19.6, 75.08) * mm, "construction": true});
            skLineSegment(sketch, "E88", {"start": v(-19.6, 58.15) * mm, "end": v(-25.96, 58.15) * mm});
            skLineSegment(sketch, "E89", {"start": v(-25.96, 58.15) * mm, "end": v(-19.6, 65.6) * mm});
            skLineSegment(sketch, "E90", {"start": v(-19.6, 65.6) * mm, "end": v(-19.6, 58.15) * mm});
            skSolve(sketch);
        }
        {
            var Q0;
            Q0 = qSketchRegion(id + "F29", true);
            var Q1;
            Q1=sQuery(id+"F29.wireOp",EDGE,"E87");
            revolve(context, id + "F30", {"entities" : qUnion([Q0]), "axis" : qUnion([Q1]), "revolveType" : RevolveType.FULL});
        }
        {
            var Q0;
            Q0=makeQuery(id+"F11.opExtrude","CAP_FACE",FACE,{"disambiguationData":[OSD([sQuery(id+"F10.wireOp",EDGE,"E62.bottom"),sQuery(id+"F10.wireOp",EDGE,"E62.top"),sQuery(id+"F10.wireOp",EDGE,"E62.left"),sQuery(id+"F10.wireOp",EDGE,"E62.right")])],"isStart":false});
            var sketch = newSketch(context, id + "F31", { "sketchPlane" : qUnion([Q0])});
            skLineSegment(sketch, "E91.bottom", {"start": v(-14.2, 14.22) * mm, "end": v(11.2, 14.22) * mm});
            skLineSegment(sketch, "E91.top", {"start": v(-14.2, -13.72) * mm, "end": v(11.2, -13.72) * mm});
            skLineSegment(sketch, "E91.left", {"start": v(-14.2, 14.22) * mm, "end": v(-14.2, -13.72) * mm});
            skLineSegment(sketch, "E91.right", {"start": v(11.2, 14.22) * mm, "end": v(11.2, -13.72) * mm});
            skLineSegment(sketch, "E92.bottom", {"start": v(-12.2, 12.22) * mm, "end": v(9.2, 12.22) * mm});
            skLineSegment(sketch, "E92.top", {"start": v(-12.2, -11.72) * mm, "end": v(9.2, -11.72) * mm});
            skLineSegment(sketch, "E92.left", {"start": v(-12.2, 12.22) * mm, "end": v(-12.2, -11.72) * mm});
            skLineSegment(sketch, "E92.right", {"start": v(9.2, 12.22) * mm, "end": v(9.2, -11.72) * mm});
            skSolve(sketch);
        }
        {
            var Q0;
            Q0 = qSketchRegion(id + "F31", true);
            extrude(context, id + "F32", {"entities" : qUnion([Q0]), "operationType" : NewBodyOperationType.ADD, "depth" : 50.8 * mm, "offsetDistance" : 25.4 * mm});
        }
        {
            var Q0;
            Q0=makeQuery(id+"F32.opExtrude","CAP_FACE",FACE,{"disambiguationData":[OSD([sQuery(id+"F31.wireOp",EDGE,"E91.bottom"),sQuery(id+"F31.wireOp",EDGE,"E91.top"),sQuery(id+"F31.wireOp",EDGE,"E91.left"),sQuery(id+"F31.wireOp",EDGE,"E91.right"),sQuery(id+"F31.wireOp",EDGE,"E92.bottom"),sQuery(id+"F31.wireOp",EDGE,"E92.top"),sQuery(id+"F31.wireOp",EDGE,"E92.left"),sQuery(id+"F31.wireOp",EDGE,"E92.right")])],"isStart":false});
            var sketch = newSketch(context, id + "F33", { "sketchPlane" : qUnion([Q0])});
            skLineSegment(sketch, "E93", {"start": v(-10.55, 15.79) * mm, "end": v(-10.55, 10.4) * mm});
            skLineSegment(sketch, "E94", {"start": v(-10.55, 10.4) * mm, "end": v(-7.46, 10.4) * mm});
            skLineSegment(sketch, "E95", {"start": v(-7.46, 10.4) * mm, "end": v(-7.46, 15.79) * mm});
            skLineSegment(sketch, "E96", {"start": v(-7.46, 15.79) * mm, "end": v(-10.55, 15.79) * mm});
            skLineSegment(sketch, "E97.1.0.0", {"start": v(-0.6, 15.79) * mm, "end": v(-3.7, 15.79) * mm});
            skLineSegment(sketch, "E97.1.0.1", {"start": v(-0.6, 10.4) * mm, "end": v(-0.6, 15.79) * mm});
            skLineSegment(sketch, "E97.1.0.2", {"start": v(-3.7, 10.4) * mm, "end": v(-0.6, 10.4) * mm});
            skLineSegment(sketch, "E97.1.0.3", {"start": v(-3.7, 15.79) * mm, "end": v(-3.7, 10.4) * mm});
            skLineSegment(sketch, "E97.2.0.0", {"start": v(6.25, 15.79) * mm, "end": v(3.17, 15.79) * mm});
            skLineSegment(sketch, "E97.2.0.1", {"start": v(6.25, 10.4) * mm, "end": v(6.25, 15.79) * mm});
            skLineSegment(sketch, "E97.2.0.2", {"start": v(3.17, 10.4) * mm, "end": v(6.25, 10.4) * mm});
            skLineSegment(sketch, "E97.2.0.3", {"start": v(3.17, 15.79) * mm, "end": v(3.17, 10.4) * mm});
            skLineSegment(sketch, "E97.direction1", {"start": v(-10.55, 10.4) * mm, "end": v(-3.7, 10.4) * mm, "construction": true});
            skLineSegment(sketch, "E98.bottom", {"start": v(-16.39, 9.07) * mm, "end": v(-9.89, 9.07) * mm});
            skLineSegment(sketch, "E98.top", {"start": v(-16.39, 5.76) * mm, "end": v(-9.89, 5.76) * mm});
            skLineSegment(sketch, "E98.left", {"start": v(-16.39, 9.07) * mm, "end": v(-16.39, 5.76) * mm});
            skLineSegment(sketch, "E98.right", {"start": v(-9.89, 9.07) * mm, "end": v(-9.89, 5.76) * mm});
            skLineSegment(sketch, "E99.1.0.0", {"start": v(-16.51, 2.03) * mm, "end": v(-16.51, -1.27) * mm});
            skLineSegment(sketch, "E99.1.0.1", {"start": v(-16.51, 2.03) * mm, "end": v(-10.01, 2.03) * mm});
            skLineSegment(sketch, "E99.1.0.2", {"start": v(-10.01, 2.03) * mm, "end": v(-10.01, -1.27) * mm});
            skLineSegment(sketch, "E99.1.0.3", {"start": v(-16.51, -1.27) * mm, "end": v(-10.01, -1.27) * mm});
            skLineSegment(sketch, "E99.2.0.0", {"start": v(-16.63, -5) * mm, "end": v(-16.63, -8.3) * mm});
            skLineSegment(sketch, "E99.2.0.1", {"start": v(-16.63, -5) * mm, "end": v(-10.14, -5) * mm});
            skLineSegment(sketch, "E99.2.0.2", {"start": v(-10.14, -5) * mm, "end": v(-10.14, -8.3) * mm});
            skLineSegment(sketch, "E99.2.0.3", {"start": v(-16.63, -8.3) * mm, "end": v(-10.14, -8.3) * mm});
            skLineSegment(sketch, "E99.direction1", {"start": v(-16.39, 5.76) * mm, "end": v(-16.51, -1.27) * mm, "construction": true});
            skLineSegment(sketch, "E100.bottom", {"start": v(-9.78, -9.98) * mm, "end": v(-6.7, -9.98) * mm});
            skLineSegment(sketch, "E100.top", {"start": v(-9.78, -15.5) * mm, "end": v(-6.7, -15.5) * mm});
            skLineSegment(sketch, "E100.left", {"start": v(-9.78, -9.98) * mm, "end": v(-9.78, -15.5) * mm});
            skLineSegment(sketch, "E100.right", {"start": v(-6.7, -9.98) * mm, "end": v(-6.7, -15.5) * mm});
            skLineSegment(sketch, "E101.1.0.0", {"start": v(-3.3, -9.99) * mm, "end": v(-3.3, -15.5) * mm});
            skLineSegment(sketch, "E101.1.0.1", {"start": v(-0.22, -9.99) * mm, "end": v(-0.22, -15.5) * mm});
            skLineSegment(sketch, "E101.1.0.2", {"start": v(-3.3, -15.5) * mm, "end": v(-0.22, -15.5) * mm});
            skLineSegment(sketch, "E101.1.0.3", {"start": v(-3.3, -9.99) * mm, "end": v(-0.22, -9.99) * mm});
            skLineSegment(sketch, "E101.2.0.0", {"start": v(3.17, -9.99) * mm, "end": v(3.17, -15.5) * mm});
            skLineSegment(sketch, "E101.2.0.1", {"start": v(6.26, -9.99) * mm, "end": v(6.26, -15.5) * mm});
            skLineSegment(sketch, "E101.2.0.2", {"start": v(3.17, -15.5) * mm, "end": v(6.26, -15.5) * mm});
            skLineSegment(sketch, "E101.2.0.3", {"start": v(3.17, -9.99) * mm, "end": v(6.26, -9.99) * mm});
            skLineSegment(sketch, "E101.direction1", {"start": v(-9.78, -15.5) * mm, "end": v(-3.3, -15.5) * mm, "construction": true});
            skPoint(sketch, "E102.firstSnap0", {"position": v(-13.14, 9.07) * mm});
            skLineSegment(sketch, "E102.bottom", {"start": v(6.63, 9.07) * mm, "end": v(14.12, 9.07) * mm});
            skLineSegment(sketch, "E102.top", {"start": v(6.63, 5.76) * mm, "end": v(14.12, 5.76) * mm});
            skLineSegment(sketch, "E102.left", {"start": v(6.63, 9.07) * mm, "end": v(6.63, 5.76) * mm});
            skLineSegment(sketch, "E102.right", {"start": v(14.12, 9.07) * mm, "end": v(14.12, 5.76) * mm});
            skLineSegment(sketch, "E103.1.0.0", {"start": v(6.6, -1.27) * mm, "end": v(14.1, -1.27) * mm});
            skLineSegment(sketch, "E103.1.0.1", {"start": v(14.1, 2.03) * mm, "end": v(14.1, -1.27) * mm});
            skLineSegment(sketch, "E103.1.0.2", {"start": v(6.6, 2.03) * mm, "end": v(6.6, -1.27) * mm});
            skLineSegment(sketch, "E103.1.0.3", {"start": v(6.6, 2.03) * mm, "end": v(14.1, 2.03) * mm});
            skLineSegment(sketch, "E103.2.0.0", {"start": v(6.57, -8.3) * mm, "end": v(14.06, -8.3) * mm});
            skLineSegment(sketch, "E103.2.0.1", {"start": v(14.06, -5) * mm, "end": v(14.06, -8.3) * mm});
            skLineSegment(sketch, "E103.2.0.2", {"start": v(6.57, -5) * mm, "end": v(6.57, -8.3) * mm});
            skLineSegment(sketch, "E103.2.0.3", {"start": v(6.57, -5) * mm, "end": v(14.06, -5) * mm});
            skLineSegment(sketch, "E103.direction1", {"start": v(6.63, 5.76) * mm, "end": v(6.6, -1.27) * mm, "construction": true});
            skSolve(sketch);
        }
        {
            var Q0;
            Q0 = qSketchRegion(id + "F33", true);
            var Q1;
            Q1 = qConstructionFilter(qBodyType(qCreatedBy(id + "F33" ,EDGE), BodyType.WIRE), ConstructionObject.NO);
            extrude(context, id + "F34", {"entities" : qUnion([Q0]), "operationType" : NewBodyOperationType.REMOVE, "surfaceEntities" : qUnion([Q1]), "oppositeDirection" : true, "depth" : 3.8 * mm, "offsetDistance" : 25.4 * mm});
        }
        {
            var Q0;
            Q0=makeQuery(id+"F5.boolean.opBoolean","MERGE",FACE,{"derivedFrom":[makeQuery(id+"F1.opExtrude","SWEPT_FACE",FACE,{"disambiguationData":[OSD([sQuery(id+"F0.wireOp",EDGE,"E0.bottom")])]}),makeQuery(id+"F5.opExtrude","SWEPT_FACE",FACE,{"disambiguationData":[OSD([sQuery(id+"F4.wireOp",EDGE,"E15")])]})]});
            var sketch = newSketch(context, id + "F35", { "sketchPlane" : qUnion([Q0])});
            skLineSegment(sketch, "E104.bottom", {"start": v(-21.1, 29.96) * mm, "end": v(-16, 29.96) * mm});
            skLineSegment(sketch, "E104.top", {"start": v(-21.1, 6.58) * mm, "end": v(-16, 6.58) * mm});
            skLineSegment(sketch, "E104.left", {"start": v(-21.1, 29.96) * mm, "end": v(-21.1, 6.58) * mm});
            skLineSegment(sketch, "E104.right", {"start": v(-16, 29.96) * mm, "end": v(-16, 6.58) * mm});
            skLineSegment(sketch, "E105.bottom", {"start": v(-7.9, 29.96) * mm, "end": v(-2.81, 29.96) * mm});
            skLineSegment(sketch, "E105.top", {"start": v(-7.9, 6.48) * mm, "end": v(-2.81, 6.48) * mm});
            skLineSegment(sketch, "E105.left", {"start": v(-7.9, 29.96) * mm, "end": v(-7.9, 6.48) * mm});
            skLineSegment(sketch, "E105.right", {"start": v(-2.81, 29.96) * mm, "end": v(-2.81, 6.48) * mm});
            skLineSegment(sketch, "E106.bottom", {"start": v(5.18, 29.96) * mm, "end": v(10.48, 29.96) * mm});
            skLineSegment(sketch, "E106.top", {"start": v(5.18, 6.48) * mm, "end": v(10.48, 6.48) * mm});
            skLineSegment(sketch, "E106.left", {"start": v(5.18, 29.96) * mm, "end": v(5.18, 6.48) * mm});
            skLineSegment(sketch, "E106.right", {"start": v(10.48, 29.96) * mm, "end": v(10.48, 6.48) * mm});
            skLineSegment(sketch, "E107.bottom", {"start": v(17.87, 29.96) * mm, "end": v(22.77, 29.96) * mm});
            skLineSegment(sketch, "E107.top", {"start": v(17.87, 6.48) * mm, "end": v(22.77, 6.48) * mm});
            skLineSegment(sketch, "E107.left", {"start": v(17.87, 29.96) * mm, "end": v(17.87, 6.48) * mm});
            skLineSegment(sketch, "E107.right", {"start": v(22.77, 29.96) * mm, "end": v(22.77, 6.48) * mm});
            skSolve(sketch);
        }
        {
            var Q0;
            Q0 = qSketchRegion(id + "F35", true);
            extrude(context, id + "F36", {"entities" : qUnion([Q0]), "operationType" : NewBodyOperationType.REMOVE, "oppositeDirection" : true, "depth" : 3 * mm, "offsetDistance" : 25.4 * mm});
        }
        {
            var Q0;
            Q0=makeQuery(id+"F5.boolean.opBoolean","MERGE",FACE,{"derivedFrom":[makeQuery(id+"F1.opExtrude","SWEPT_FACE",FACE,{"disambiguationData":[OSD([sQuery(id+"F0.wireOp",EDGE,"E0.top")])]}),makeQuery(id+"F5.opExtrude","SWEPT_FACE",FACE,{"disambiguationData":[OSD([sQuery(id+"F4.wireOp",EDGE,"E18.MirrorCS")])]})]});
            var sketch = newSketch(context, id + "F37", { "sketchPlane" : qUnion([Q0])});
            skLineSegment(sketch, "E108.bottom", {"start": v(17.12, 29.97) * mm, "end": v(22.37, 29.97) * mm});
            skLineSegment(sketch, "E108.top", {"start": v(17.12, 5.75) * mm, "end": v(22.37, 5.75) * mm});
            skLineSegment(sketch, "E108.left", {"start": v(17.12, 29.97) * mm, "end": v(17.12, 5.75) * mm});
            skLineSegment(sketch, "E108.right", {"start": v(22.37, 29.97) * mm, "end": v(22.37, 5.75) * mm});
            skLineSegment(sketch, "E109.bottom", {"start": v(2.82, 30.27) * mm, "end": v(8.75, 30.27) * mm});
            skLineSegment(sketch, "E109.top", {"start": v(2.82, 5.56) * mm, "end": v(8.75, 5.56) * mm});
            skLineSegment(sketch, "E109.left", {"start": v(2.82, 30.27) * mm, "end": v(2.82, 5.56) * mm});
            skLineSegment(sketch, "E109.right", {"start": v(8.75, 30.27) * mm, "end": v(8.75, 5.56) * mm});
            skLineSegment(sketch, "E110.MirrorCS", {"start": v(-17.12, 29.97) * mm, "end": v(-17.12, 5.75) * mm});
            skPoint(sketch, "E111.orphan", {"position": v(-8.75, 30.27) * mm});
            skPoint(sketch, "E112.MirrorCS.start.orphan", {"position": v(-2.82, 30.27) * mm});
            skLineSegment(sketch, "E113.MirrorCS", {"start": v(-2.82, 30.27) * mm, "end": v(-8.75, 30.27) * mm});
            skLineSegment(sketch, "E114.MirrorCS", {"start": v(-2.82, 5.56) * mm, "end": v(-8.75, 5.56) * mm});
            skLineSegment(sketch, "E115.MirrorCS", {"start": v(-2.82, 30.27) * mm, "end": v(-2.82, 5.56) * mm});
            skLineSegment(sketch, "E116.MirrorCS", {"start": v(-8.75, 30.27) * mm, "end": v(-8.75, 5.56) * mm});
            skLineSegment(sketch, "E117.MirrorCS", {"start": v(-17.12, 5.75) * mm, "end": v(-22.37, 5.75) * mm});
            skLineSegment(sketch, "E118.MirrorCS", {"start": v(-22.37, 29.97) * mm, "end": v(-22.37, 5.75) * mm});
            skLineSegment(sketch, "E119.MirrorCS", {"start": v(-17.12, 29.97) * mm, "end": v(-22.37, 29.97) * mm});
            skSolve(sketch);
        }
        {
            var Q0;
            Q0 = qSketchRegion(id + "F37", true);
            extrude(context, id + "F38", {"entities" : qUnion([Q0]), "operationType" : NewBodyOperationType.REMOVE, "oppositeDirection" : true, "depth" : 3 * mm, "offsetDistance" : 25.4 * mm});
        }
        {
            var Q0;
            Q0=makeQuery(id+"F5.boolean.opBoolean","MERGE",FACE,{"derivedFrom":[makeQuery(id+"F1.opExtrude","SWEPT_FACE",FACE,{"disambiguationData":[OSD([sQuery(id+"F0.wireOp",EDGE,"E0.left")])]}),makeQuery(id+"F5.opExtrude","SWEPT_FACE",FACE,{"disambiguationData":[OSD([sQuery(id+"F4.wireOp",EDGE,"E26.MirrorCS")])]})]});
            var sketch = newSketch(context, id + "F39", { "sketchPlane" : qUnion([Q0])});
            skLineSegment(sketch, "E120.bottom", {"start": v(-24.62, 30.57) * mm, "end": v(-18.25, 30.57) * mm});
            skLineSegment(sketch, "E120.top", {"start": v(-24.62, 4.13) * mm, "end": v(-18.25, 4.13) * mm});
            skLineSegment(sketch, "E120.left", {"start": v(-24.62, 30.57) * mm, "end": v(-24.62, 4.13) * mm});
            skLineSegment(sketch, "E120.right", {"start": v(-18.25, 30.57) * mm, "end": v(-18.25, 4.13) * mm});
            skLineSegment(sketch, "E121.bottom", {"start": v(-9.17, 30.03) * mm, "end": v(-3.47, 30.03) * mm});
            skLineSegment(sketch, "E121.top", {"start": v(-9.17, 4.13) * mm, "end": v(-3.47, 4.13) * mm});
            skLineSegment(sketch, "E121.left", {"start": v(-9.17, 30.03) * mm, "end": v(-9.17, 4.13) * mm});
            skLineSegment(sketch, "E121.right", {"start": v(-3.47, 30.03) * mm, "end": v(-3.47, 4.13) * mm});
            skLineSegment(sketch, "E122.MirrorCS", {"start": v(9.17, 30.03) * mm, "end": v(3.47, 30.03) * mm});
            skLineSegment(sketch, "E123.MirrorCS", {"start": v(3.47, 30.03) * mm, "end": v(3.47, 4.13) * mm});
            skLineSegment(sketch, "E124.MirrorCS", {"start": v(9.17, 30.03) * mm, "end": v(9.17, 4.13) * mm});
            skLineSegment(sketch, "E125.MirrorCS", {"start": v(9.17, 4.13) * mm, "end": v(3.47, 4.13) * mm});
            skLineSegment(sketch, "E126.MirrorCS", {"start": v(18.25, 30.57) * mm, "end": v(18.25, 4.13) * mm});
            skLineSegment(sketch, "E127.MirrorCS", {"start": v(24.62, 30.57) * mm, "end": v(18.25, 30.57) * mm});
            skLineSegment(sketch, "E128.MirrorCS", {"start": v(24.62, 30.57) * mm, "end": v(24.62, 4.13) * mm});
            skLineSegment(sketch, "E129.MirrorCS", {"start": v(24.62, 4.13) * mm, "end": v(18.25, 4.13) * mm});
            skSolve(sketch);
        }
        {
            var Q0;
            Q0 = qSketchRegion(id + "F39", true);
            extrude(context, id + "F40", {"entities" : qUnion([Q0]), "operationType" : NewBodyOperationType.REMOVE, "oppositeDirection" : true, "depth" : 3 * mm, "offsetDistance" : 25.4 * mm});
        }
        {
            var Q0;
            Q0=makeQuery(id+"F32.opExtrude","SWEPT_FACE",FACE,{"disambiguationData":[OSD([sQuery(id+"F31.wireOp",EDGE,"E91.left")])]});
            var sketch = newSketch(context, id + "F41", { "sketchPlane" : qUnion([Q0])});
            skCircle(sketch, "E130", {"center": v(0, 59.13) * mm, "radius": 7.24 * mm});
            skSolve(sketch);
        }
        {
            var Q0;
            Q0 = qSketchRegion(id + "F41", true);
            extrude(context, id + "F42", {"entities" : qUnion([Q0]), "operationType" : NewBodyOperationType.REMOVE, "oppositeDirection" : true, "depth" : 35.05 * mm, "offsetDistance" : 25.4 * mm});
        }
        {
            var Q0;
            Q0=makeQuery(id+"F5.boolean.opBoolean","MERGE",FACE,{"derivedFrom":[makeQuery(id+"F1.opExtrude","SWEPT_FACE",FACE,{"disambiguationData":[OSD([sQuery(id+"F0.wireOp",EDGE,"E0.right")])]}),makeQuery(id+"F5.opExtrude","SWEPT_FACE",FACE,{"disambiguationData":[OSD([sQuery(id+"F4.wireOp",EDGE,"E23")])]})]});
            var sketch = newSketch(context, id + "F43", { "sketchPlane" : qUnion([Q0])});
            skLineSegment(sketch, "E131", {"start": v(-9.37, 0) * mm, "end": v(6.5, 0) * mm});
            skLineSegment(sketch, "E132", {"start": v(6.5, 0) * mm, "end": v(6.5, 13.21) * mm});
            skLineSegment(sketch, "E133", {"start": v(-9.37, 0) * mm, "end": v(-9.37, 13.36) * mm});
            skArc(sketch, "E134", {"start": v(6.5, 13.21) * mm, "mid": v(-1.36, 21.29) * mm, "end": v(-9.37, 13.36) * mm});
            skArc(sketch, "E135", {"start": v(4.97, 13.4) * mm, "mid": v(-1.25, 19.76) * mm, "end": v(-7.73, 13.66) * mm});
            skLineSegment(sketch, "E136", {"start": v(-7.73, 13.66) * mm, "end": v(-7.73, 0.5) * mm});
            skLineSegment(sketch, "E137", {"start": v(-7.73, 0.5) * mm, "end": v(4.97, 0.5) * mm});
            skLineSegment(sketch, "E138", {"start": v(4.97, 0.5) * mm, "end": v(4.97, 13.4) * mm});
            skSolve(sketch);
        }
        {
            var Q0;
            Q0 = qSketchRegion(id + "F43", true);
            extrude(context, id + "F44", {"entities" : qUnion([Q0]), "operationType" : NewBodyOperationType.ADD, "depth" : 2 * mm, "offsetDistance" : 25.4 * mm});
        }
    });
